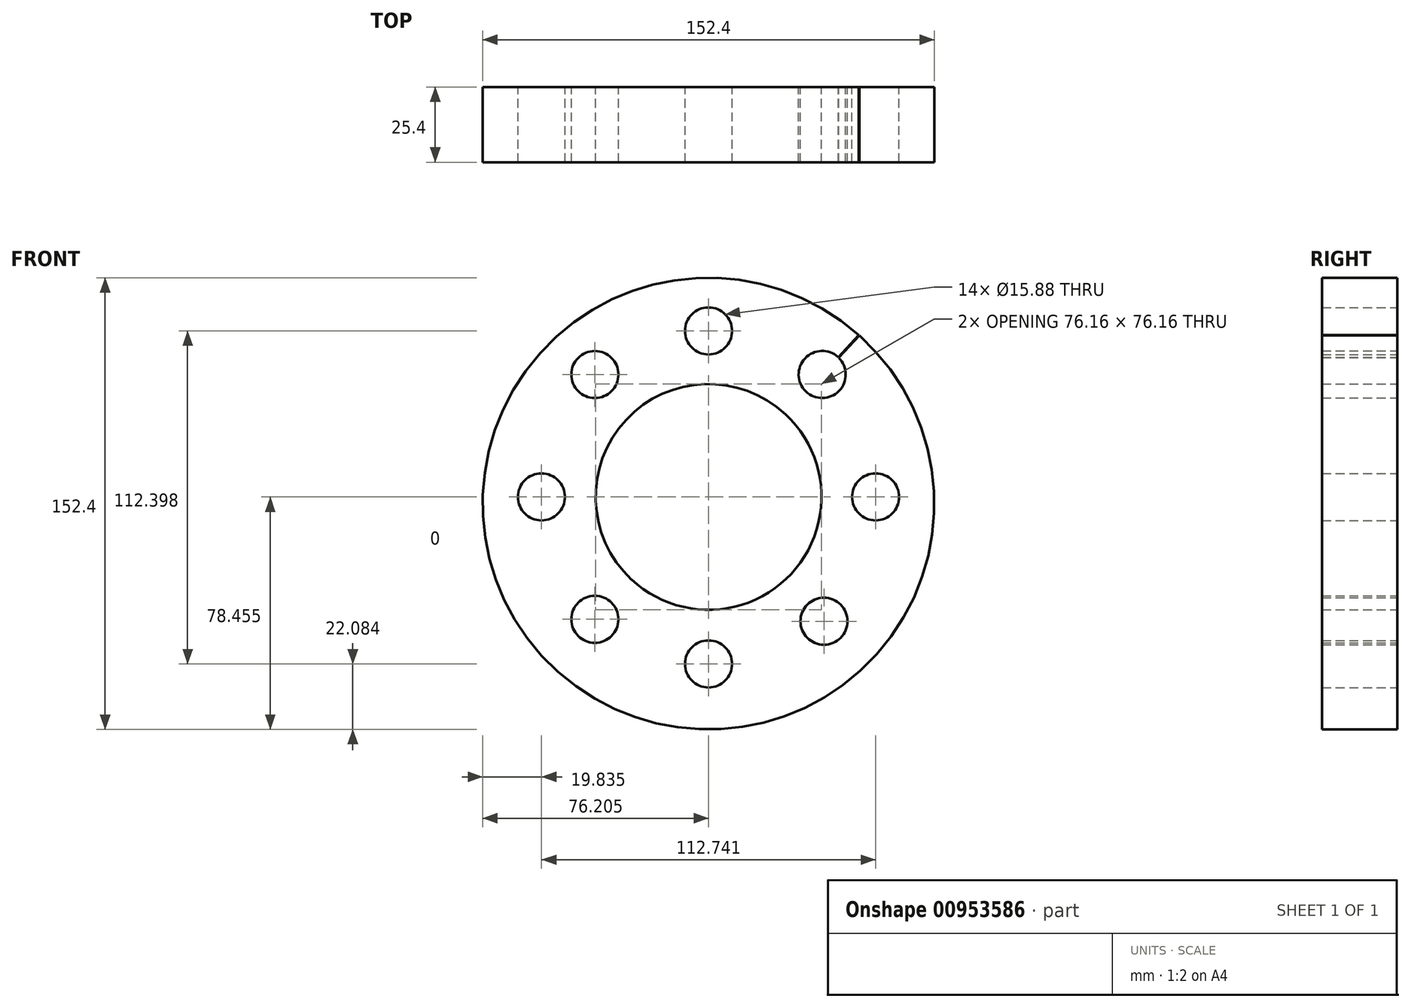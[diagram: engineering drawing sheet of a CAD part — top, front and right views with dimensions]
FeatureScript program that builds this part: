
annotation { "Feature Type Name" : "Feature", "Feature Type Description" : "" }
export const myFeature = defineFeature(function(context is Context, id is Id, definition is map)
    precondition{}
    {
        {
            var Q0;
            Q0=qCreatedBy(makeId("Front.planeOp"),FACE);
            var sketch = newSketch(context, id + "F0", { "sketchPlane" : qUnion([Q0])});
            skCircle(sketch, "E0", {"center": v(0, 0) * mm, "radius": 38.1 * mm});
            skCircle(sketch, "E1", {"center": v(0, -2.26) * mm, "radius": 76.2 * mm});
            skLineSegment(sketch, "E2", {"start": v(0, 38.1) * mm, "end": v(0, 73.94) * mm});
            skCircle(sketch, "E3", {"center": v(0, 56.02) * mm, "radius": 7.94 * mm});
            skCircle(sketch, "E4", {"center": v(0, 0) * mm, "radius": 56.37 * mm});
            skLineSegment(sketch, "E5", {"start": v(0, 0) * mm, "end": v(25.98, 27.87) * mm});
            skLineSegment(sketch, "E6", {"start": v(25.96, 28.02) * mm, "end": v(51.94, 55.9) * mm});
            skCircle(sketch, "E7", {"center": v(38.35, 41.31) * mm, "radius": 7.94 * mm});
            skCircle(sketch, "E8", {"center": v(56.38, 0) * mm, "radius": 7.94 * mm});
            skLineSegment(sketch, "E9.MirrorCS", {"start": v(26.14, 27.86) * mm, "end": v(52.12, 55.73) * mm});
            skCircle(sketch, "E10.MirrorC", {"center": v(0.01, -0.01) * mm, "radius": 38.1 * mm});
            skLineSegment(sketch, "E11.MirrorCS", {"start": v(0, 0) * mm, "end": v(-25.98, 27.87) * mm});
            skLineSegment(sketch, "E12.MirrorCS", {"start": v(-25.96, 28.02) * mm, "end": v(-51.94, 55.9) * mm});
            skCircle(sketch, "E13", {"center": v(-38.35, 41.3) * mm, "radius": 7.94 * mm});
            skCircle(sketch, "E14", {"center": v(-56.37, 0) * mm, "radius": 7.94 * mm});
            skLineSegment(sketch, "E15.MirrorCS", {"start": v(0, 0) * mm, "end": v(25.98, -27.87) * mm});
            skLineSegment(sketch, "E16.MirrorCS", {"start": v(25.96, -28.02) * mm, "end": v(51.94, -55.9) * mm});
            skLineSegment(sketch, "E17.MirrorCS", {"start": v(0, 0) * mm, "end": v(-25.98, -27.87) * mm});
            skLineSegment(sketch, "E18.MirrorCS", {"start": v(-25.96, -28.02) * mm, "end": v(-51.94, -55.9) * mm});
            skCircle(sketch, "E19", {"center": v(-38.35, -41.31) * mm, "radius": 7.94 * mm});
            skCircle(sketch, "E20", {"center": v(0, -56.38) * mm, "radius": 7.94 * mm});
            skCircle(sketch, "E21", {"center": v(38.95, -41.96) * mm, "radius": 7.94 * mm});
            skSolve(sketch);
        }
        {
            var Q0;
            {var subQ6=sQuery(id+"F0.wireOp",EDGE,"E9.MirrorCS");var subQ21=sQuery(id+"F0.wireOp",EDGE,"E1");var subQ22=makeQuery(id+"F0.imprint","INTERSECT",VERTEX,{"derivedFrom":[subQ21,subQ6]});Q0=makeQuery(id+"F0.imprint","IMPRINT",FACE,{"disambiguationData":[TD([[makeQuery(id+"F0.imprint","IMPRINT",EDGE,{"disambiguationData":[TD([[subQ22,1.0]])],"derivedFrom":subQ21}),1.0]])]});}
            var Q1;
            {var subQ8=sQuery(id+"F0.wireOp",EDGE,"E0");var subQ35=makeQuery(id+"F0.imprint","IMPRINT",VERTEX,{"derivedFrom":subQ8});Q1=makeQuery(id+"F0.imprint","IMPRINT",FACE,{"disambiguationData":[TD([[makeQuery(id+"F0.imprint","IMPRINT",EDGE,{"disambiguationData":[TD([[subQ35,-1.0]])],"derivedFrom":subQ8}),-1.0]])]});}
            var Q2;
            {var subQ5=sQuery(id+"F0.wireOp",EDGE,"E2");var subQ7=sQuery(id+"F0.wireOp",EDGE,"E1");var subQ8=makeQuery(id+"F0.imprint","INTERSECT",VERTEX,{"derivedFrom":[subQ7,subQ5]});Q2=makeQuery(id+"F0.imprint","IMPRINT",FACE,{"disambiguationData":[TD([[makeQuery(id+"F0.imprint","IMPRINT",EDGE,{"disambiguationData":[TD([[subQ8,1.0]])],"derivedFrom":subQ7}),1.0]])]});}
            var Q3;
            {var subQ5=sQuery(id+"F0.wireOp",EDGE,"E2");var subQ7=sQuery(id+"F0.wireOp",EDGE,"E1");var subQ8=makeQuery(id+"F0.imprint","INTERSECT",VERTEX,{"derivedFrom":[subQ7,subQ5]});Q3=makeQuery(id+"F0.imprint","IMPRINT",FACE,{"disambiguationData":[TD([[makeQuery(id+"F0.imprint","IMPRINT",EDGE,{"disambiguationData":[TD([[subQ8,-1.0]])],"derivedFrom":subQ7}),1.0]])]});}
            extrude(context, id + "F1", {"entities" : qUnion([Q0, Q1, Q2, Q3]), "depth" : 25.4 * mm, "offsetDistance" : 25.4 * mm});
        }
    });
